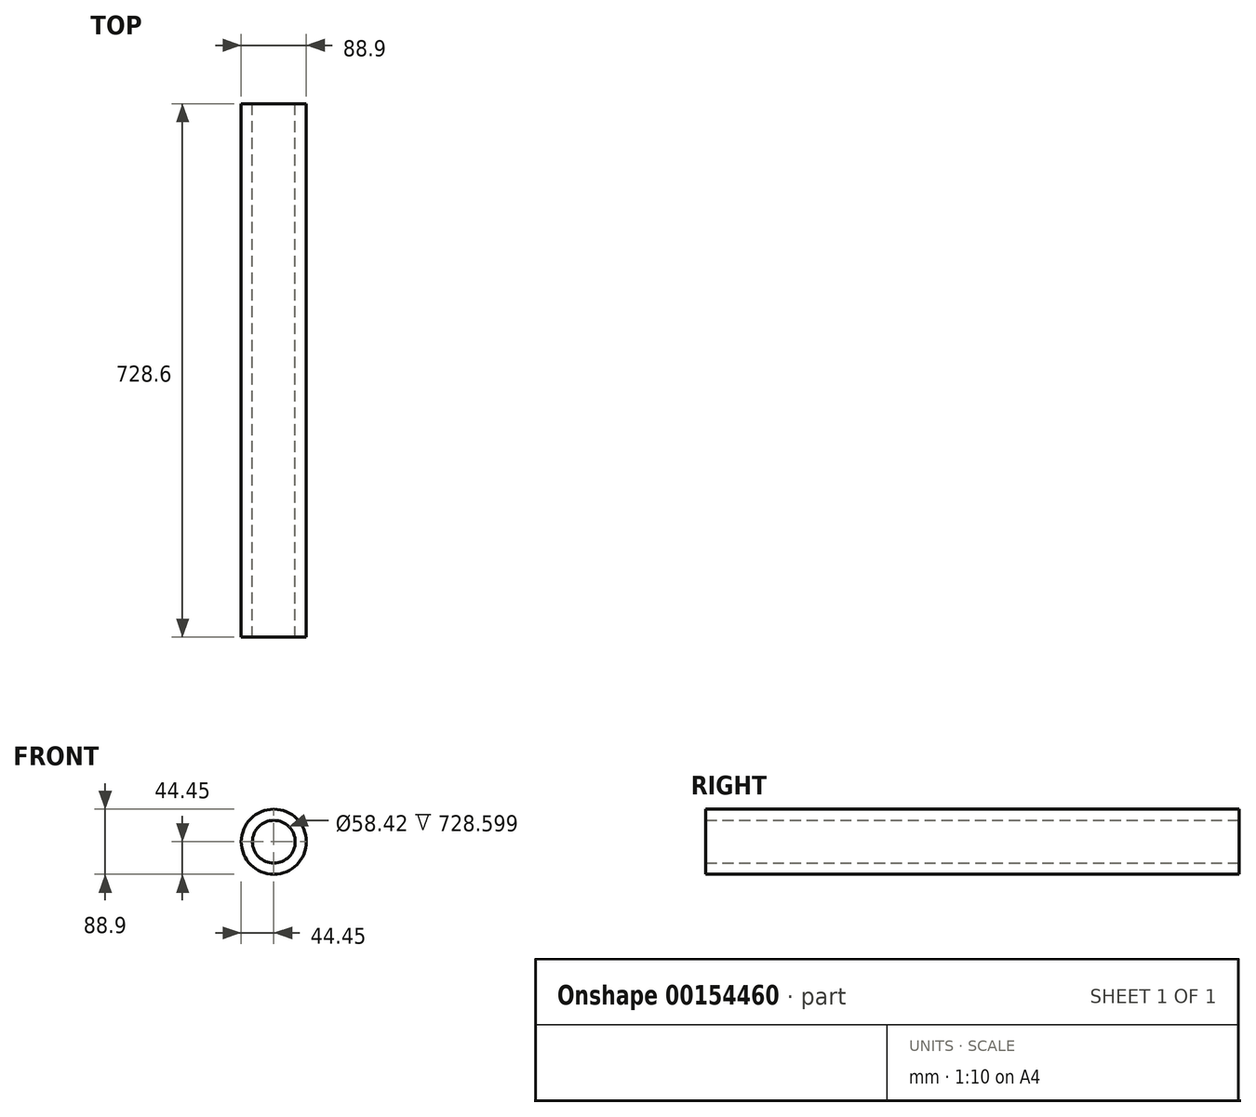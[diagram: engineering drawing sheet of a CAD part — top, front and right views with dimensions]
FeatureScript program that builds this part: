
annotation { "Feature Type Name" : "Feature", "Feature Type Description" : "" }
export const myFeature = defineFeature(function(context is Context, id is Id, definition is map)
    precondition{}
    {
        {
            var Q0;
            Q0=qCreatedBy(makeId("Front.planeOp"),FACE);
            var sketch = newSketch(context, id + "F0", { "sketchPlane" : qUnion([Q0])});
            skCircle(sketch, "E0", {"center": v(0, 0) * mm, "radius": 44.45 * mm});
            skCircle(sketch, "E1.0", {"center": v(0, 0) * mm, "radius": 29.21 * mm});
            skSolve(sketch);
        }
        {
            var Q0;
            Q0=makeQuery(id+"F0.imprint","IMPRINT",FACE,{"disambiguationData":[TD([[makeQuery(id+"F0.imprint","IMPRINT",EDGE,{"derivedFrom":sQuery(id+"F0.wireOp",EDGE,"E0")}),1.0]])]});
            extrude(context, id + "F1", {"entities" : qUnion([Q0]), "depth" : 728.6 * mm});
        }
    });
